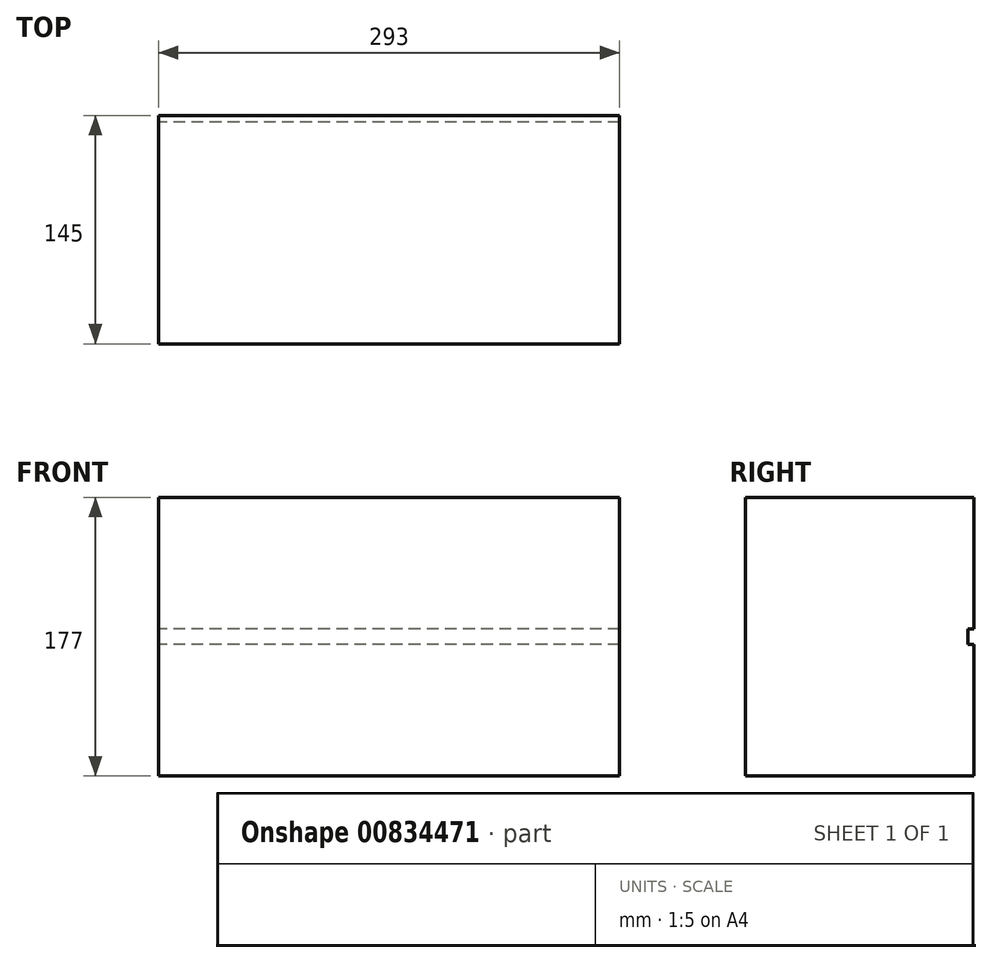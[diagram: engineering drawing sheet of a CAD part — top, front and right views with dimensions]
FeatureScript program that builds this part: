
annotation { "Feature Type Name" : "Feature", "Feature Type Description" : "" }
export const myFeature = defineFeature(function(context is Context, id is Id, definition is map)
    precondition{}
    {
        {
            var Q0;
            Q0=qCreatedBy(makeId("Top.planeOp"),FACE);
            var sketch = newSketch(context, id + "F0", { "sketchPlane" : qUnion([Q0])});
            skLineSegment(sketch, "E0.bottom", {"start": v(0, 0) * mm, "end": v(285, 0) * mm});
            skLineSegment(sketch, "E0.top", {"start": v(0, -141) * mm, "end": v(285, -141) * mm});
            skLineSegment(sketch, "E0.left", {"start": v(0, 0) * mm, "end": v(0, -141) * mm});
            skLineSegment(sketch, "E0.right", {"start": v(285, 0) * mm, "end": v(285, -141) * mm});
            skSolve(sketch);
        }
        {
            var Q0;
            Q0 = qSketchRegion(id + "F0", true);
            extrude(context, id + "F1", {"entities" : qUnion([Q0]), "depth" : 169 * mm, "offsetDistance" : 25.4 * mm});
        }
        {
            var Q0;
            Q0=makeQuery(id+"F1.opExtrude","SWEPT_FACE",FACE,{"disambiguationData":[OSD([sQuery(id+"F0.wireOp",EDGE,"E0.right")])]});
            var sketch = newSketch(context, id + "F2", { "sketchPlane" : qUnion([Q0])});
            skLineSegment(sketch, "E1.bottom", {"start": v(-141, 169) * mm, "end": v(0, 169) * mm});
            skLineSegment(sketch, "E1.top", {"start": v(-141, 0) * mm, "end": v(0, 0) * mm});
            skLineSegment(sketch, "E1.left", {"start": v(-141, 169) * mm, "end": v(-141, 0) * mm});
            skLineSegment(sketch, "E1.right", {"start": v(0, 169) * mm, "end": v(0, 0) * mm});
            skSolve(sketch);
        }
        {
            var Q0;
            Q0 = qSketchRegion(id + "F2", true);
            extrude(context, id + "F3", {"entities" : qUnion([Q0]), "depth" : 4 * mm, "offsetDistance" : 25.4 * mm});
        }
        {
            var Q0;
            Q0=makeQuery(id+"F1.opExtrude","SWEPT_FACE",FACE,{"disambiguationData":[OSD([sQuery(id+"F0.wireOp",EDGE,"E0.left")])]});
            var sketch = newSketch(context, id + "F4", { "sketchPlane" : qUnion([Q0])});
            skLineSegment(sketch, "E2.bottom", {"start": v(0, 0) * mm, "end": v(141, 0) * mm});
            skLineSegment(sketch, "E2.top", {"start": v(0, 169) * mm, "end": v(141, 169) * mm});
            skLineSegment(sketch, "E2.left", {"start": v(0, 0) * mm, "end": v(0, 169) * mm});
            skLineSegment(sketch, "E2.right", {"start": v(141, 0) * mm, "end": v(141, 169) * mm});
            skSolve(sketch);
        }
        {
            var Q0;
            Q0 = qSketchRegion(id + "F4", true);
            extrude(context, id + "F5", {"entities" : qUnion([Q0]), "depth" : 4 * mm, "offsetDistance" : 25.4 * mm});
        }
        {
            var Q0;
            Q0=makeQuery(id+"F1.opExtrude","CAP_FACE",FACE,{"disambiguationData":[OSD([sQuery(id+"F0.wireOp",EDGE,"E0.bottom"),sQuery(id+"F0.wireOp",EDGE,"E0.top"),sQuery(id+"F0.wireOp",EDGE,"E0.left"),sQuery(id+"F0.wireOp",EDGE,"E0.right")])],"isStart":false});
            var sketch = newSketch(context, id + "F6", { "sketchPlane" : qUnion([Q0])});
            skLineSegment(sketch, "E3.bottom", {"start": v(-4, -141) * mm, "end": v(289, -141) * mm});
            skLineSegment(sketch, "E3.top", {"start": v(-4, 0) * mm, "end": v(289, 0) * mm});
            skLineSegment(sketch, "E3.left", {"start": v(-4, -141) * mm, "end": v(-4, 0) * mm});
            skLineSegment(sketch, "E3.right", {"start": v(289, -141) * mm, "end": v(289, 0) * mm});
            skSolve(sketch);
        }
        {
            var Q0;
            Q0 = qSketchRegion(id + "F6", true);
            extrude(context, id + "F7", {"entities" : qUnion([Q0]), "operationType" : NewBodyOperationType.ADD, "depth" : 4 * mm, "offsetDistance" : 25.4 * mm});
        }
        {
            var Q0;
            Q0=makeQuery(id+"F1.opExtrude","CAP_FACE",FACE,{"disambiguationData":[OSD([sQuery(id+"F0.wireOp",EDGE,"E0.bottom"),sQuery(id+"F0.wireOp",EDGE,"E0.top"),sQuery(id+"F0.wireOp",EDGE,"E0.left"),sQuery(id+"F0.wireOp",EDGE,"E0.right")])],"isStart":true});
            var sketch = newSketch(context, id + "F8", { "sketchPlane" : qUnion([Q0])});
            skLineSegment(sketch, "E4.bottom", {"start": v(-4, 141) * mm, "end": v(289, 141) * mm});
            skLineSegment(sketch, "E4.top", {"start": v(-4, 0) * mm, "end": v(289, 0) * mm});
            skLineSegment(sketch, "E4.left", {"start": v(-4, 141) * mm, "end": v(-4, 0) * mm});
            skLineSegment(sketch, "E4.right", {"start": v(289, 141) * mm, "end": v(289, 0) * mm});
            skSolve(sketch);
        }
        {
            var Q0;
            Q0 = qSketchRegion(id + "F8", true);
            extrude(context, id + "F9", {"entities" : qUnion([Q0]), "operationType" : NewBodyOperationType.ADD, "depth" : 4 * mm, "offsetDistance" : 25.4 * mm});
        }
        {
            var Q0;
            Q0=makeQuery(id+"F1.opExtrude","SWEPT_FACE",FACE,{"disambiguationData":[OSD([sQuery(id+"F0.wireOp",EDGE,"E0.bottom")])]});
            var sketch = newSketch(context, id + "F10", { "sketchPlane" : qUnion([Q0])});
            skLineSegment(sketch, "E5.bottom", {"start": v(-289, 173) * mm, "end": v(4, 173) * mm});
            skLineSegment(sketch, "E5.top", {"start": v(-289, 89.5) * mm, "end": v(4, 89.5) * mm});
            skLineSegment(sketch, "E5.left", {"start": v(-289, 173) * mm, "end": v(-289, 89.5) * mm});
            skLineSegment(sketch, "E5.right", {"start": v(4, 173) * mm, "end": v(4, 89.5) * mm});
            skLineSegment(sketch, "E6.bottom", {"start": v(-289, 79.5) * mm, "end": v(4, 79.5) * mm});
            skLineSegment(sketch, "E6.top", {"start": v(-289, -4) * mm, "end": v(4, -4) * mm});
            skLineSegment(sketch, "E6.left", {"start": v(-289, 79.5) * mm, "end": v(-289, -4) * mm});
            skLineSegment(sketch, "E6.right", {"start": v(4, 79.5) * mm, "end": v(4, -4) * mm});
            skSolve(sketch);
        }
        {
            var Q0;
            Q0 = qSketchRegion(id + "F10", true);
            extrude(context, id + "F11", {"entities" : qUnion([Q0]), "operationType" : NewBodyOperationType.ADD, "depth" : 4 * mm, "offsetDistance" : 25.4 * mm});
        }
    });
